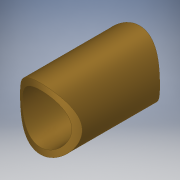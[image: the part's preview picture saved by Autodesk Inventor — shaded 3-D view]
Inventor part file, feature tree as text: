
AUTODESK INVENTOR PART (.ipt)
format: ipt  version: 2018 (Build 220112000, 112)  size: 121,856 bytes
history: native  units: in
note: dims shown in document units (in); Inventor stores cm internally (conversion verified against a paired STEP export)
features: extrude x2, sketch x2
ambient origin geometry x8: Origin, YZ Plane, XZ Plane, XY Plane, X Axis, Y Axis, Z Axis, Center Point
bodies: Solid1 (feature_tree)
feature tree (4):
  extrude  "Extrusion1"  Depth=0.25in
  extrude  "Extrusion2"  Depth=0.156in
  sketch  "Sketch1"  dims[d0=0.312in d1=0.25in]
  sketch  "Sketch2"  dims[d2=0.5in d3=0.0in d4=0.5in d5=0.156in d6=0.75in d7=0.5in d8=0.0in]
